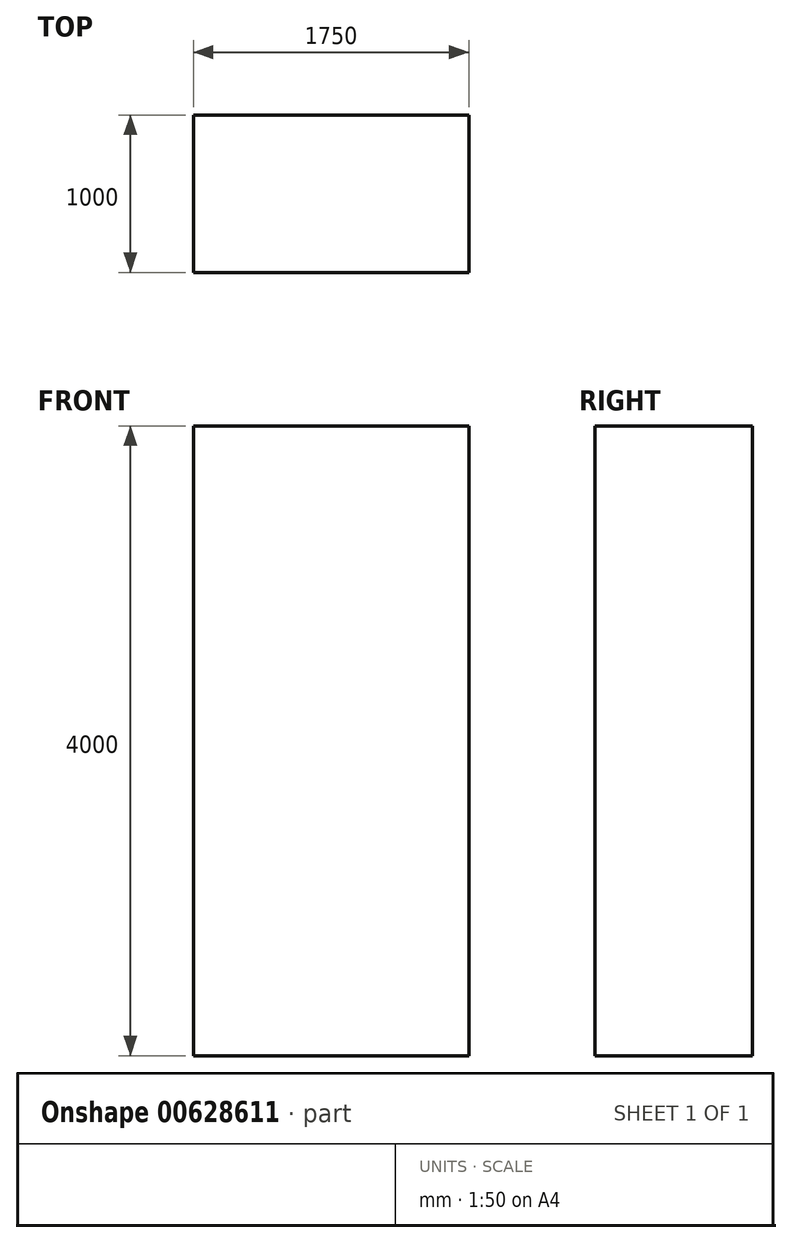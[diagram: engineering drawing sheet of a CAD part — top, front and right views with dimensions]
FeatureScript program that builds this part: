
annotation { "Feature Type Name" : "Feature", "Feature Type Description" : "" }
export const myFeature = defineFeature(function(context is Context, id is Id, definition is map)
    precondition{}
    {
        {
            var Q0;
            Q0=qCreatedBy(makeId("Front.planeOp"),FACE);
            var sketch = newSketch(context, id + "F0", { "sketchPlane" : qUnion([Q0])});
            skLineSegment(sketch, "E0.bottom", {"start": v(875, 2000) * mm, "end": v(-875, 2000) * mm});
            skLineSegment(sketch, "E0.top", {"start": v(875, -2000) * mm, "end": v(-875, -2000) * mm});
            skLineSegment(sketch, "E0.left", {"start": v(875, 2000) * mm, "end": v(875, -2000) * mm});
            skLineSegment(sketch, "E0.right", {"start": v(-875, 2000) * mm, "end": v(-875, -2000) * mm});
            skPoint(sketch, "E0.middle", {"position": v(0, 0) * mm});
            skSolve(sketch);
        }
        {
            var Q0;
            Q0 = qSketchRegion(id + "F0", true);
            extrude(context, id + "F1", {"entities" : qUnion([Q0]), "depth" : 1000 * mm, "offsetDistance" : 25.4 * mm});
        }
    });
